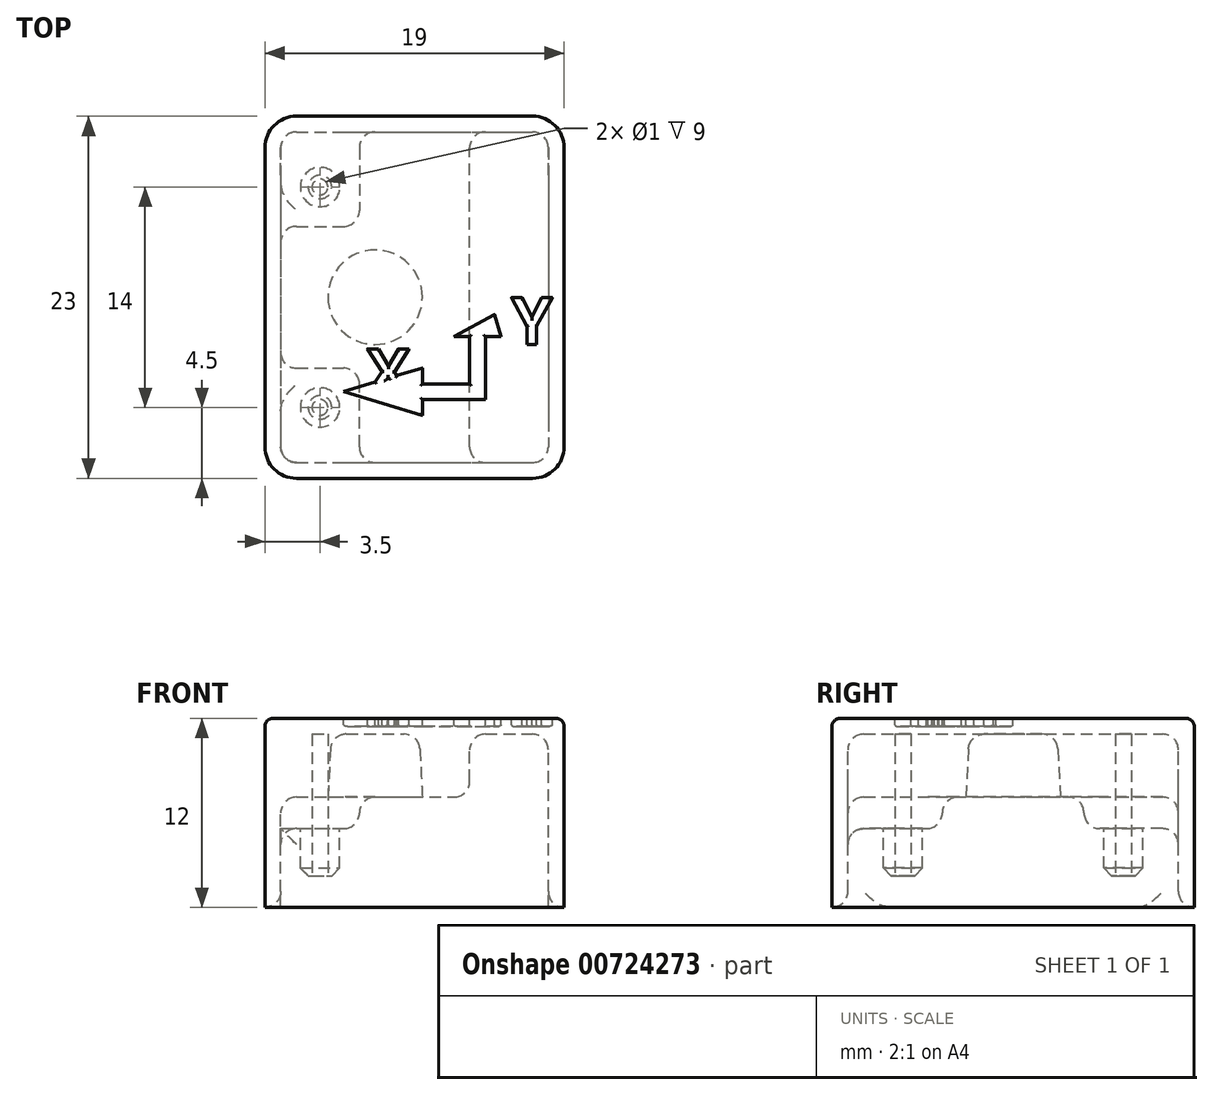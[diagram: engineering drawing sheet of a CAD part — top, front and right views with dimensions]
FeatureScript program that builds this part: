
annotation { "Feature Type Name" : "Feature", "Feature Type Description" : "" }
export const myFeature = defineFeature(function(context is Context, id is Id, definition is map)
    precondition{}
    {
        {
            var Q0;
            Q0=qCreatedBy(makeId("Top.planeOp"),FACE);
            var sketch = newSketch(context, id + "F0", { "sketchPlane" : qUnion([Q0])});
            skLineSegment(sketch, "E0.bottom", {"start": v(-9.5, 11.5) * mm, "end": v(9.5, 11.5) * mm});
            skLineSegment(sketch, "E0.top", {"start": v(-9.5, -11.5) * mm, "end": v(9.5, -11.5) * mm});
            skLineSegment(sketch, "E0.left", {"start": v(-9.5, 11.5) * mm, "end": v(-9.5, -11.5) * mm});
            skLineSegment(sketch, "E0.right", {"start": v(9.5, 11.5) * mm, "end": v(9.5, -11.5) * mm});
            skLineSegment(sketch, "E1", {"start": v(-9.5, 0) * mm, "end": v(9.5, 0) * mm, "construction": true});
            skSolve(sketch);
        }
        {
            var Q0;
            Q0 = qSketchRegion(id + "F0", true);
            extrude(context, id + "F1", {"entities" : qUnion([Q0]), "oppositeDirection" : true, "depth" : 12 * mm, "offsetDistance" : 25 * mm});
        }
        {
            var Q0;
            Q0=makeQuery(id+"F1.opExtrude","CAP_FACE",FACE,{"disambiguationData":[OSD([sQuery(id+"F0.wireOp",EDGE,"E0.bottom"),sQuery(id+"F0.wireOp",EDGE,"E0.top"),sQuery(id+"F0.wireOp",EDGE,"E0.left"),sQuery(id+"F0.wireOp",EDGE,"E0.right")])],"isStart":false});
            shell(context, id + "F2", {"entities" : qUnion([Q0]), "thickness" : 1 * mm});
        }
        {
            var Q0;
            Q0=makeQuery(id+"F2.opShell","OFFSET_FACE",FACE,{"disambiguationData":[OSD([sQuery(id+"F0.wireOp",EDGE,"E0.bottom"),sQuery(id+"F0.wireOp",EDGE,"E0.top"),sQuery(id+"F0.wireOp",EDGE,"E0.left"),sQuery(id+"F0.wireOp",EDGE,"E0.right")])]});
            var sketch = newSketch(context, id + "F3", { "sketchPlane" : qUnion([Q0])});
            skLineSegment(sketch, "E2.bottom", {"start": v(3.5, 10.5) * mm, "end": v(-8.5, 10.5) * mm});
            skLineSegment(sketch, "E2.top", {"start": v(3.5, -10.5) * mm, "end": v(-8.5, -10.5) * mm});
            skLineSegment(sketch, "E2.left", {"start": v(3.5, 10.5) * mm, "end": v(3.5, -10.5) * mm});
            skLineSegment(sketch, "E2.right", {"start": v(-8.5, 10.5) * mm, "end": v(-8.5, -10.5) * mm});
            skSolve(sketch);
        }
        {
            var Q0;
            Q0 = qSketchRegion(id + "F3", true);
            extrude(context, id + "F4", {"entities" : qUnion([Q0]), "operationType" : NewBodyOperationType.ADD, "depth" : 4 * mm, "offsetDistance" : 25 * mm});
        }
        {
            var Q0;
            Q0=makeQuery(id+"F4.opExtrude","CAP_FACE",FACE,{"disambiguationData":[OSD([sQuery(id+"F3.wireOp",EDGE,"E2.bottom"),sQuery(id+"F3.wireOp",EDGE,"E2.top"),sQuery(id+"F3.wireOp",EDGE,"E2.left"),sQuery(id+"F3.wireOp",EDGE,"E2.right")])],"isStart":false});
            var sketch = newSketch(context, id + "F5", { "sketchPlane" : qUnion([Q0])});
            skLineSegment(sketch, "E3.bottom", {"start": v(-8.5, 10.5) * mm, "end": v(-3.5, 10.5) * mm});
            skLineSegment(sketch, "E3.top", {"start": v(-8.5, 4.5) * mm, "end": v(-3.5, 4.5) * mm});
            skLineSegment(sketch, "E3.left", {"start": v(-8.5, 10.5) * mm, "end": v(-8.5, 4.5) * mm});
            skLineSegment(sketch, "E3.right", {"start": v(-3.5, 10.5) * mm, "end": v(-3.5, 4.5) * mm});
            skLineSegment(sketch, "E4.bottom", {"start": v(-8.5, -10.5) * mm, "end": v(-3.5, -10.5) * mm});
            skLineSegment(sketch, "E4.top", {"start": v(-8.5, -4.5) * mm, "end": v(-3.5, -4.5) * mm});
            skLineSegment(sketch, "E4.left", {"start": v(-8.5, -10.5) * mm, "end": v(-8.5, -4.5) * mm});
            skLineSegment(sketch, "E4.right", {"start": v(-3.5, -10.5) * mm, "end": v(-3.5, -4.5) * mm});
            skSolve(sketch);
        }
        {
            var Q0;
            Q0 = qSketchRegion(id + "F5", true);
            extrude(context, id + "F6", {"entities" : qUnion([Q0]), "operationType" : NewBodyOperationType.ADD, "depth" : 2 * mm, "offsetDistance" : 25 * mm});
        }
        {
            var Q0;
            Q0=makeQuery(id+"F6.opExtrude","CAP_FACE",FACE,{"disambiguationData":[OSD([sQuery(id+"F5.wireOp",EDGE,"E3.bottom"),sQuery(id+"F5.wireOp",EDGE,"E3.top"),sQuery(id+"F5.wireOp",EDGE,"E3.left"),sQuery(id+"F5.wireOp",EDGE,"E3.right")])],"isStart":false});
            var sketch = newSketch(context, id + "F7", { "sketchPlane" : qUnion([Q0])});
            skCircle(sketch, "E5", {"center": v(-6, 7) * mm, "radius": 1.25 * mm});
            skCircle(sketch, "E6", {"center": v(-6, -7) * mm, "radius": 1.25 * mm});
            skLineSegment(sketch, "E7", {"start": v(0, 0) * mm, "end": v(-9.5, 0) * mm, "construction": true});
            skSolve(sketch);
        }
        {
            var Q0;
            Q0=makeQuery(id+"F7.imprint","IMPRINT",FACE,{"disambiguationData":[TD([[makeQuery(id+"F7.imprint","IMPRINT",EDGE,{"derivedFrom":sQuery(id+"F7.wireOp",EDGE,"E5")}),1.0]])]});
            var Q1;
            Q1=makeQuery(id+"F7.imprint","IMPRINT",FACE,{"disambiguationData":[TD([[makeQuery(id+"F7.imprint","IMPRINT",EDGE,{"derivedFrom":sQuery(id+"F7.wireOp",EDGE,"E6")}),1.0]])]});
            extrude(context, id + "F8", {"entities" : qUnion([Q0, Q1]), "operationType" : NewBodyOperationType.ADD, "depth" : 3 * mm, "offsetDistance" : 25 * mm});
        }
        {
            var Q0;
            Q0=makeQuery(id+"F8.opExtrude","CAP_EDGE",EDGE,{"disambiguationData":[OSD([sQuery(id+"F7.wireOp",EDGE,"E5")])],"isStart":false});
            var Q1;
            Q1=makeQuery(id+"F8.opExtrude","CAP_EDGE",EDGE,{"disambiguationData":[OSD([sQuery(id+"F7.wireOp",EDGE,"E6")])],"isStart":false});
            chamfer(context, id + "F9", {"entities" : qUnion([Q0, Q1]), "width" : 0.5 * mm, "tangentPropagation" : true});
        }
        {
            var Q0;
            Q0=makeQuery(id+"F2.opShell","OFFSET_FACE",FACE,{"disambiguationData":[OSD([sQuery(id+"F0.wireOp",EDGE,"E0.bottom"),sQuery(id+"F0.wireOp",EDGE,"E0.top"),sQuery(id+"F0.wireOp",EDGE,"E0.left"),sQuery(id+"F0.wireOp",EDGE,"E0.right")])]});
            var Q1;
            Q1=makeQuery(id+"F2.opShell","OFFSET_FACE",FACE,{"disambiguationData":[OSD([sQuery(id+"F0.wireOp",EDGE,"E0.top")])]});
            var Q2;
            Q2=makeQuery(id+"F4.opExtrude","CAP_FACE",FACE,{"disambiguationData":[OSD([sQuery(id+"F3.wireOp",EDGE,"E2.bottom"),sQuery(id+"F3.wireOp",EDGE,"E2.top"),sQuery(id+"F3.wireOp",EDGE,"E2.left"),sQuery(id+"F3.wireOp",EDGE,"E2.right")])],"isStart":false});
            var Q3;
            Q3=makeQuery(id+"F6.opExtrude","SWEPT_EDGE",EDGE,{"disambiguationData":[OSD([sQuery(id+"F3.wireOp",EDGE,"E2.right"),sQuery(id+"F5.wireOp",EDGE,"E3.top"),sQuery(id+"F5.wireOp",EDGE,"E3.left")])]});
            var Q4;
            Q4=makeQuery(id+"F6.opExtrude","SWEPT_FACE",FACE,{"disambiguationData":[OSD([sQuery(id+"F5.wireOp",EDGE,"E3.top")])]});
            var Q5;
            Q5=makeQuery(id+"F6.opExtrude","SWEPT_FACE",FACE,{"disambiguationData":[OSD([sQuery(id+"F5.wireOp",EDGE,"E3.right")])]});
            var Q6;
            Q6=makeQuery(id+"F2.opShell","OFFSET_FACE",FACE,{"disambiguationData":[OSD([sQuery(id+"F0.wireOp",EDGE,"E0.bottom")])]});
            var Q7;
            Q7=makeQuery(id+"F6.opExtrude","SWEPT_FACE",FACE,{"disambiguationData":[OSD([sQuery(id+"F5.wireOp",EDGE,"E4.top")])]});
            var Q8;
            Q8=makeQuery(id+"F6.opExtrude","CAP_EDGE",EDGE,{"disambiguationData":[OSD([sQuery(id+"F5.wireOp",EDGE,"E4.right")])],"isStart":false});
            var Q9;
            {var subQ0=sQuery(id+"F0.wireOp",EDGE,"E0.bottom");Q9=makeQuery(id+"F2.opShell","OFFSET_EDGE",EDGE,{"disambiguationData":[OSD([subQ0]),TDD([makeQuery(id+"F1.opExtrude","CAP_EDGE",EDGE,{"disambiguationData":[OSD([subQ0])],"isStart":false})])]});}
            fillet(context, id + "F10", {"entities" : qUnion([Q0, Q1, Q2, Q3, Q4, Q5, Q6, Q7, Q8, Q9]), "radius" : 1 * mm, "tangentPropagation" : true, "allowEdgeOverflow" : false});
        }
        {
            var Q0;
            Q0=makeQuery(id+"F4.opExtrude","CAP_FACE",FACE,{"disambiguationData":[OSD([sQuery(id+"F3.wireOp",EDGE,"E2.bottom"),sQuery(id+"F3.wireOp",EDGE,"E2.top"),sQuery(id+"F3.wireOp",EDGE,"E2.left"),sQuery(id+"F3.wireOp",EDGE,"E2.right")])],"isStart":false});
            var sketch = newSketch(context, id + "F11", { "sketchPlane" : qUnion([Q0])});
            skCircle(sketch, "E8", {"center": v(-2.5, 0) * mm, "radius": 3 * mm});
            skLineSegment(sketch, "E9", {"start": v(0, 0) * mm, "end": v(-2.5, 0) * mm, "construction": true});
            skSolve(sketch);
        }
        {
            var Q0;
            Q0 = qSketchRegion(id + "F11", true);
            extrude(context, id + "F12", {"entities" : qUnion([Q0]), "operationType" : NewBodyOperationType.REMOVE, "oppositeDirection" : true, "depth" : 4 * mm, "offsetDistance" : 25 * mm, "hasDraft" : true, "draftAngle" : 3 * degree, "draftPullDirection" : true});
        }
        {
            var Q0;
            Q0=makeQuery(id+"F12.boolean.opBoolean","COPY",FACE,{"derivedFrom":makeQuery(id+"F12.opExtrude","CAP_FACE",FACE,{"disambiguationData":[OSD([sQuery(id+"F11.wireOp",EDGE,"E8")])],"isStart":false})});
            var Q1;
            Q1=makeQuery(id+"F12.boolean.opBoolean","COPY",EDGE,{"derivedFrom":makeQuery(id+"F12.opExtrude","CAP_EDGE",EDGE,{"disambiguationData":[OSD([sQuery(id+"F11.wireOp",EDGE,"E8")])],"isStart":true})});
            fillet(context, id + "F13", {"entities" : qUnion([Q0, Q1]), "radius" : 1 * mm, "tangentPropagation" : true, "allowEdgeOverflow" : false});
        }
        {
            var Q0;
            Q0=makeQuery(id+"F1.opExtrude","SWEPT_EDGE",EDGE,{"disambiguationData":[OSD([sQuery(id+"F0.wireOp",EDGE,"E0.top"),sQuery(id+"F0.wireOp",EDGE,"E0.right")])]});
            var Q1;
            Q1=makeQuery(id+"F1.opExtrude","SWEPT_EDGE",EDGE,{"disambiguationData":[OSD([sQuery(id+"F0.wireOp",EDGE,"E0.top"),sQuery(id+"F0.wireOp",EDGE,"E0.left")])]});
            var Q2;
            Q2=makeQuery(id+"F1.opExtrude","SWEPT_EDGE",EDGE,{"disambiguationData":[OSD([sQuery(id+"F0.wireOp",EDGE,"E0.bottom"),sQuery(id+"F0.wireOp",EDGE,"E0.left")])]});
            var Q3;
            Q3=makeQuery(id+"F1.opExtrude","SWEPT_EDGE",EDGE,{"disambiguationData":[OSD([sQuery(id+"F0.wireOp",EDGE,"E0.bottom"),sQuery(id+"F0.wireOp",EDGE,"E0.right")])]});
            fillet(context, id + "F14", {"entities" : qUnion([Q0, Q1, Q2, Q3]), "radius" : 2 * mm, "tangentPropagation" : true, "allowEdgeOverflow" : false});
        }
        {
            var Q0;
            Q0=makeQuery(id+"F1.opExtrude","CAP_FACE",FACE,{"disambiguationData":[OSD([sQuery(id+"F0.wireOp",EDGE,"E0.bottom"),sQuery(id+"F0.wireOp",EDGE,"E0.top"),sQuery(id+"F0.wireOp",EDGE,"E0.left"),sQuery(id+"F0.wireOp",EDGE,"E0.right")])],"isStart":true});
            var sketch = newSketch(context, id + "F15", { "sketchPlane" : qUnion([Q0])});
            skLineSegment(sketch, "E10", {"start": v(0.5, -7.5) * mm, "end": v(-4.5, -6) * mm});
            skLineSegment(sketch, "E11", {"start": v(-4.5, -6) * mm, "end": v(0.5, -4.5) * mm});
            skLineSegment(sketch, "E12", {"start": v(0.5, -4.5) * mm, "end": v(0.5, -5.5) * mm});
            skLineSegment(sketch, "E13", {"start": v(0.5, -6.5) * mm, "end": v(4.5, -6.5) * mm});
            skLineSegment(sketch, "E14", {"start": v(3.5, -5.5) * mm, "end": v(0.5, -5.5) * mm});
            skLineSegment(sketch, "E15", {"start": v(3.5, -5.5) * mm, "end": v(3.5, -2.5) * mm});
            skLineSegment(sketch, "E16", {"start": v(3.5, -2.5) * mm, "end": v(2.5, -2.5) * mm});
            skLineSegment(sketch, "E17", {"start": v(2.5, -2.5) * mm, "end": v(7.08, 0) * mm});
            skLineSegment(sketch, "E18", {"start": v(4, 2.5) * mm, "end": v(5.5, -2.5) * mm});
            skLineSegment(sketch, "E19", {"start": v(5.5, -2.5) * mm, "end": v(4.5, -2.5) * mm});
            skLineSegment(sketch, "E20", {"start": v(4.5, -2.5) * mm, "end": v(4.5, -6.5) * mm});
            skLineSegment(sketch, "E21.trimOffspring", {"start": v(0.5, -6.5) * mm, "end": v(0.5, -7.5) * mm});
            skText(sketch, "E22", { "text": "X", "fontName": "OpenSans-Bold.ttf"});
            skText(sketch, "E23", { "text": "Y", "fontName": "OpenSans-Bold.ttf"});
            const initialGuessF15  = {"E22": [-0.00305, -0.00626, 1, 0, 0.003], "E23": [0.00615, -0.003, 1, 0, 0.003]};
            skSetInitialGuess(sketch, initialGuessF15);
            skSolve(sketch);
        }
        {
            var Q0;
            Q0 = qSketchRegion(id + "F15", true);
            extrude(context, id + "F16", {"entities" : qUnion([Q0]), "operationType" : NewBodyOperationType.REMOVE, "oppositeDirection" : true, "depth" : 0.5 * mm, "offsetDistance" : 25 * mm});
        }
        {
            var Q0;
            Q0=makeQuery(id+"F16.boolean.opBoolean","COPY",FACE,{"derivedFrom":makeQuery(id+"F16.opExtrude","CAP_FACE",FACE,{"disambiguationData":[OSD([sQuery(id+"F15.wireOp",EDGE,"E10"),sQuery(id+"F15.wireOp",EDGE,"E11"),sQuery(id+"F15.wireOp",EDGE,"E12"),sQuery(id+"F15.wireOp",EDGE,"E13"),sQuery(id+"F15.wireOp",EDGE,"E14"),sQuery(id+"F15.wireOp",EDGE,"E15"),sQuery(id+"F15.wireOp",EDGE,"E16"),sQuery(id+"F15.wireOp",EDGE,"E17"),sQuery(id+"F15.wireOp",EDGE,"E18"),sQuery(id+"F15.wireOp",EDGE,"E19"),sQuery(id+"F15.wireOp",EDGE,"E20"),sQuery(id+"F15.wireOp",EDGE,"E21.trimOffspring")])],"isStart":false})});
            var Q1;
            Q1=makeQuery(id+"F16.boolean.opBoolean","COPY",FACE,{"derivedFrom":makeQuery(id+"F16.opExtrude","CAP_FACE",FACE,{"disambiguationData":[OSD([sQuery(id+"F15.wireOp",EDGE,"E22.sketch_text.stroke-0"),sQuery(id+"F15.wireOp",EDGE,"E22.sketch_text.stroke-1"),sQuery(id+"F15.wireOp",EDGE,"E22.sketch_text.stroke-2"),sQuery(id+"F15.wireOp",EDGE,"E22.sketch_text.stroke-3"),sQuery(id+"F15.wireOp",EDGE,"E22.sketch_text.stroke-4"),sQuery(id+"F15.wireOp",EDGE,"E22.sketch_text.stroke-5"),sQuery(id+"F15.wireOp",EDGE,"E22.sketch_text.stroke-6"),sQuery(id+"F15.wireOp",EDGE,"E22.sketch_text.stroke-7"),sQuery(id+"F15.wireOp",EDGE,"E22.sketch_text.stroke-8"),sQuery(id+"F15.wireOp",EDGE,"E22.sketch_text.stroke-9"),sQuery(id+"F15.wireOp",EDGE,"E22.sketch_text.stroke-10"),sQuery(id+"F15.wireOp",EDGE,"E22.sketch_text.stroke-11")])],"isStart":false})});
            var Q2;
            Q2=makeQuery(id+"F16.boolean.opBoolean","COPY",FACE,{"derivedFrom":makeQuery(id+"F16.opExtrude","CAP_FACE",FACE,{"disambiguationData":[OSD([sQuery(id+"F15.wireOp",EDGE,"E23.sketch_text.stroke-0"),sQuery(id+"F15.wireOp",EDGE,"E23.sketch_text.stroke-1"),sQuery(id+"F15.wireOp",EDGE,"E23.sketch_text.stroke-2"),sQuery(id+"F15.wireOp",EDGE,"E23.sketch_text.stroke-3"),sQuery(id+"F15.wireOp",EDGE,"E23.sketch_text.stroke-4"),sQuery(id+"F15.wireOp",EDGE,"E23.sketch_text.stroke-5"),sQuery(id+"F15.wireOp",EDGE,"E23.sketch_text.stroke-6"),sQuery(id+"F15.wireOp",EDGE,"E23.sketch_text.stroke-7"),sQuery(id+"F15.wireOp",EDGE,"E23.sketch_text.stroke-8")])],"isStart":false})});
            fillet(context, id + "F17", {"entities" : qUnion([Q0, Q1, Q2]), "radius" : 0.1 * mm, "tangentPropagation" : true, "allowEdgeOverflow" : false});
        }
        {
            var Q0;
            Q0=makeQuery(id+"F1.opExtrude","CAP_EDGE",EDGE,{"disambiguationData":[OSD([sQuery(id+"F0.wireOp",EDGE,"E0.left")])],"isStart":true});
            var Q1;
            {var subQ0=sQuery(id+"F0.wireOp",EDGE,"E0.left");var subQ1=sQuery(id+"F0.wireOp",EDGE,"E0.bottom");Q1=makeQuery(id+"F14.opFillet","BLEND_EDGE",EDGE,{"blendedFrom":[makeQuery(id+"F1.opExtrude","SWEPT_EDGE",EDGE,{"disambiguationData":[OSD([subQ1,subQ0])]}),makeQuery(id+"F1.opExtrude","CAP_FACE",FACE,{"disambiguationData":[OSD([subQ1,sQuery(id+"F0.wireOp",EDGE,"E0.top"),subQ0,sQuery(id+"F0.wireOp",EDGE,"E0.right")])],"isStart":true})],"blendedInto":[makeQuery(id+"F1.opExtrude","CAP_FACE",FACE,{"disambiguationData":[OSD([subQ1,sQuery(id+"F0.wireOp",EDGE,"E0.top"),subQ0,sQuery(id+"F0.wireOp",EDGE,"E0.right")])],"isStart":true})]});}
            var Q2;
            Q2=makeQuery(id+"F1.opExtrude","CAP_EDGE",EDGE,{"disambiguationData":[OSD([sQuery(id+"F0.wireOp",EDGE,"E0.bottom")])],"isStart":true});
            fillet(context, id + "F18", {"entities" : qUnion([Q0, Q1, Q2]), "radius" : 0.5 * mm, "tangentPropagation" : true, "allowEdgeOverflow" : false});
        }
        {
            var Q0;
            Q0=makeQuery(id+"F16.boolean.opBoolean","COPY",EDGE,{"derivedFrom":makeQuery(id+"F16.opExtrude","CAP_EDGE",EDGE,{"disambiguationData":[OSD([sQuery(id+"F15.wireOp",EDGE,"E11")])],"isStart":true})});
            var Q1;
            Q1=makeQuery(id+"F16.boolean.opBoolean","COPY",EDGE,{"derivedFrom":makeQuery(id+"F16.opExtrude","CAP_EDGE",EDGE,{"disambiguationData":[OSD([sQuery(id+"F15.wireOp",EDGE,"E10")])],"isStart":true})});
            var Q2;
            Q2=makeQuery(id+"F16.boolean.opBoolean","COPY",EDGE,{"derivedFrom":makeQuery(id+"F16.opExtrude","CAP_EDGE",EDGE,{"disambiguationData":[OSD([sQuery(id+"F15.wireOp",EDGE,"E21.trimOffspring")])],"isStart":true})});
            var Q3;
            Q3=makeQuery(id+"F16.boolean.opBoolean","COPY",EDGE,{"derivedFrom":makeQuery(id+"F16.opExtrude","CAP_EDGE",EDGE,{"disambiguationData":[OSD([sQuery(id+"F15.wireOp",EDGE,"E13")])],"isStart":true})});
            var Q4;
            Q4=makeQuery(id+"F16.boolean.opBoolean","COPY",EDGE,{"derivedFrom":makeQuery(id+"F16.opExtrude","CAP_EDGE",EDGE,{"disambiguationData":[OSD([sQuery(id+"F15.wireOp",EDGE,"E12")])],"isStart":true})});
            var Q5;
            Q5=makeQuery(id+"F16.boolean.opBoolean","COPY",EDGE,{"derivedFrom":makeQuery(id+"F16.opExtrude","CAP_EDGE",EDGE,{"disambiguationData":[OSD([sQuery(id+"F15.wireOp",EDGE,"E14")])],"isStart":true})});
            var Q6;
            Q6=makeQuery(id+"F16.boolean.opBoolean","COPY",EDGE,{"derivedFrom":makeQuery(id+"F16.opExtrude","CAP_EDGE",EDGE,{"disambiguationData":[OSD([sQuery(id+"F15.wireOp",EDGE,"E15")])],"isStart":true})});
            var Q7;
            Q7=makeQuery(id+"F16.boolean.opBoolean","COPY",EDGE,{"derivedFrom":makeQuery(id+"F16.opExtrude","CAP_EDGE",EDGE,{"disambiguationData":[OSD([sQuery(id+"F15.wireOp",EDGE,"E17")])],"isStart":true})});
            var Q8;
            Q8=makeQuery(id+"F16.boolean.opBoolean","COPY",EDGE,{"derivedFrom":makeQuery(id+"F16.opExtrude","CAP_EDGE",EDGE,{"disambiguationData":[OSD([sQuery(id+"F15.wireOp",EDGE,"E16")])],"isStart":true})});
            var Q9;
            Q9=makeQuery(id+"F16.boolean.opBoolean","COPY",EDGE,{"derivedFrom":makeQuery(id+"F16.opExtrude","CAP_EDGE",EDGE,{"disambiguationData":[OSD([sQuery(id+"F15.wireOp",EDGE,"E18")])],"isStart":true})});
            var Q10;
            Q10=makeQuery(id+"F16.boolean.opBoolean","COPY",EDGE,{"derivedFrom":makeQuery(id+"F16.opExtrude","CAP_EDGE",EDGE,{"disambiguationData":[OSD([sQuery(id+"F15.wireOp",EDGE,"E19")])],"isStart":true})});
            var Q11;
            Q11=makeQuery(id+"F16.boolean.opBoolean","COPY",EDGE,{"derivedFrom":makeQuery(id+"F16.opExtrude","CAP_EDGE",EDGE,{"disambiguationData":[OSD([sQuery(id+"F15.wireOp",EDGE,"E20")])],"isStart":true})});
            fillet(context, id + "F19", {"entities" : qUnion([Q0, Q1, Q2, Q3, Q4, Q5, Q6, Q7, Q8, Q9, Q10, Q11]), "radius" : 0.2 * mm, "tangentPropagation" : true, "allowEdgeOverflow" : false});
        }
        {
            var Q0;
            Q0=makeQuery(id+"F8.opExtrude","CAP_FACE",FACE,{"disambiguationData":[OSD([sQuery(id+"F7.wireOp",EDGE,"E5")])],"isStart":false});
            var sketch = newSketch(context, id + "F20", { "sketchPlane" : qUnion([Q0])});
            skCircle(sketch, "E24", {"center": v(-6, 7) * mm, "radius": 0.5 * mm});
            skCircle(sketch, "E25", {"center": v(-6, -7) * mm, "radius": 0.5 * mm});
            skSolve(sketch);
        }
        {
            var Q0;
            Q0=makeQuery(id+"F20.imprint","IMPRINT",FACE,{"disambiguationData":[TD([[makeQuery(id+"F20.imprint","IMPRINT",EDGE,{"derivedFrom":sQuery(id+"F20.wireOp",EDGE,"E24")}),1.0]])]});
            var Q1;
            Q1=makeQuery(id+"F20.imprint","IMPRINT",FACE,{"disambiguationData":[TD([[makeQuery(id+"F20.imprint","IMPRINT",EDGE,{"derivedFrom":sQuery(id+"F20.wireOp",EDGE,"E25")}),1.0]])]});
            extrude(context, id + "F21", {"entities" : qUnion([Q0, Q1]), "operationType" : NewBodyOperationType.REMOVE, "oppositeDirection" : true, "depth" : 9 * mm, "offsetDistance" : 25 * mm});
        }
    });
